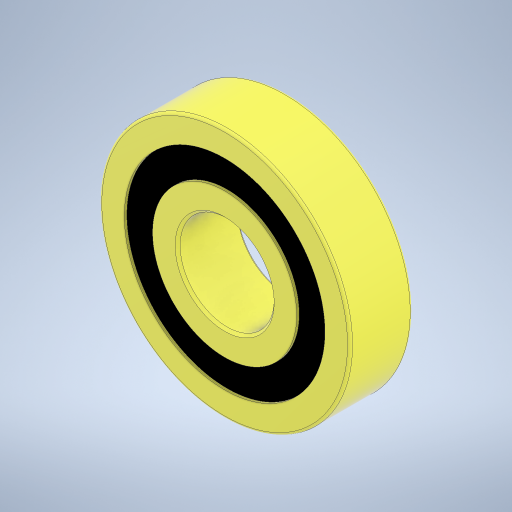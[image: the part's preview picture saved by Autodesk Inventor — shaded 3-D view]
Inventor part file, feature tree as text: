
AUTODESK INVENTOR PART (.ipt)
format: ipt  version: 2024 (Build 280153000, 153)  size: 319,488 bytes
history: native  units: in
note: dims shown in document units (in); Inventor stores cm internally (conversion verified against a paired STEP export)
features: extrude x2, chamfer x2, sketch x2, fillet x1, plane x1, direct_edit x1, projected_geometry x1, other x1
ambient origin geometry x8: Origin, YZ Plane, XZ Plane, XY Plane, X Axis, Y Axis, Z Axis, Center Point
bodies: Solid1 (feature_tree)
feature tree (11):
  extrude  "Extrusion1"  Depth=0.05in
  fillet  "Fillet1"  Radius=0.05in
  chamfer  "Chamfer1"  Distance=0.125in
  chamfer  "Chamfer2"  Distance=0.005in
  plane  "Work Plane1"
  extrude  "Extrusion2"  Depth=0.3937in TaperAngle=45.0deg
  direct_edit  "Direct Edit1"
  sketch  "Sketch1"  dims[d0=0.1875in d1=0.5in d2=0.05in]
  sketch  "Sketch2"  dims[d3=0.05in d4=0.125in d5=0.0in d6=0.005in d7=0.005in d8=0.125in d9=45.0deg d10=0.005in d11=0.125in d12=45.0deg d13=0.115in d14=0.0in d15=3.937in d16=0.3937in d17=0.3937in]
  projected_geometry  "Project Cut Edges1"
  other  "Scale1"
